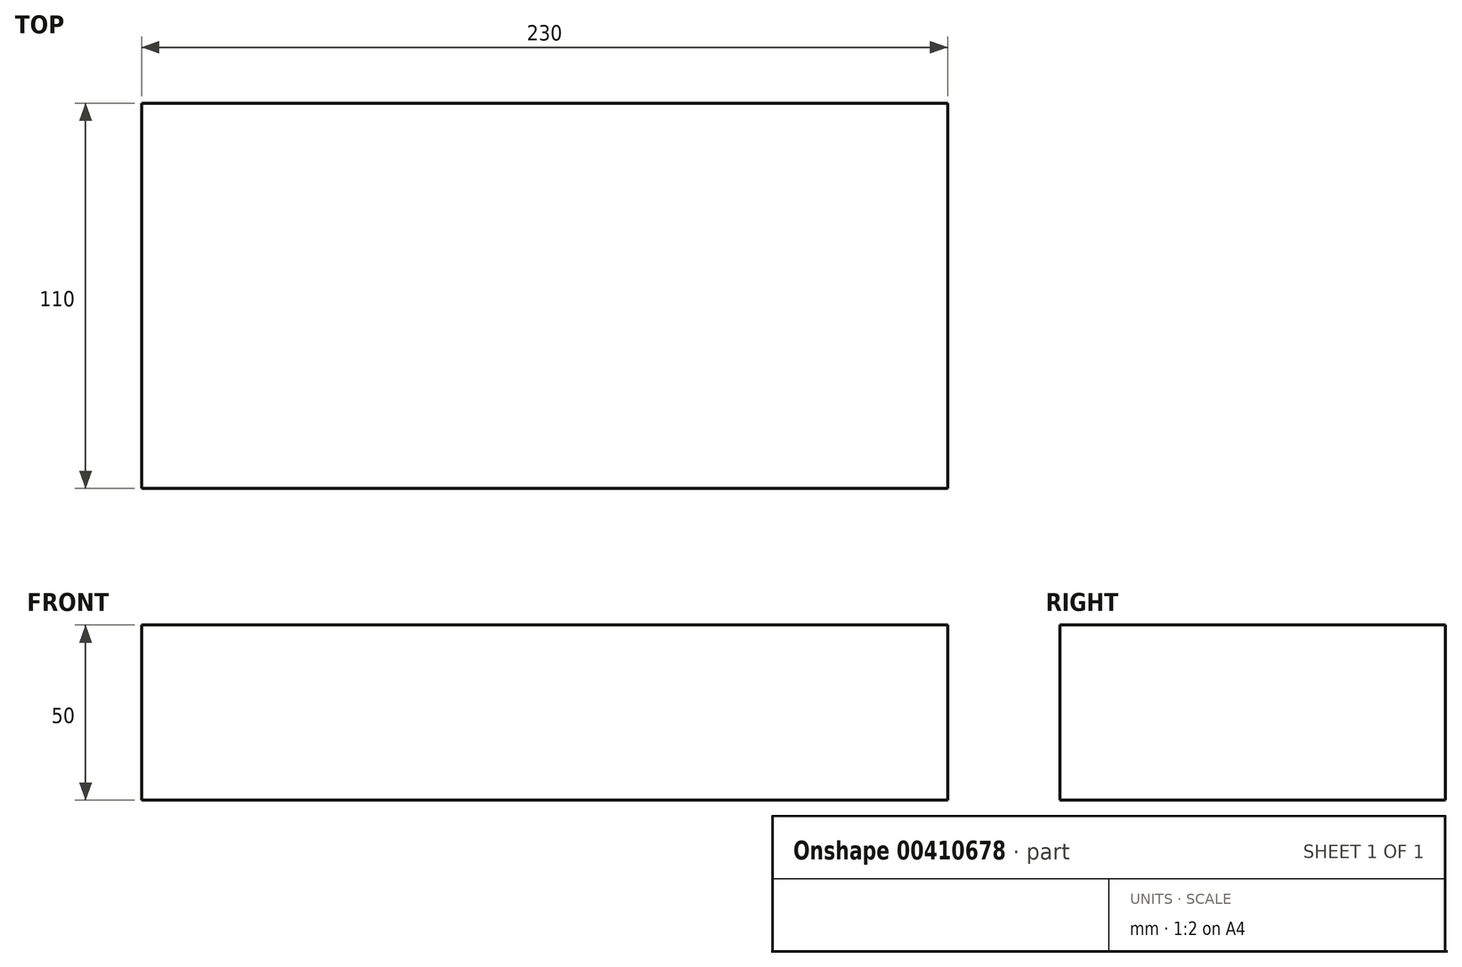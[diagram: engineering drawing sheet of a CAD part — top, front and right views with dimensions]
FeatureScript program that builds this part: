
annotation { "Feature Type Name" : "Feature", "Feature Type Description" : "" }
export const myFeature = defineFeature(function(context is Context, id is Id, definition is map)
    precondition{}
    {
        {
            var Q0;
            Q0=qCreatedBy(makeId("Front.planeOp"),FACE);
            var sketch = newSketch(context, id + "F0", { "sketchPlane" : qUnion([Q0])});
            skLineSegment(sketch, "E0.bottom", {"start": v(115, 25) * mm, "end": v(-115, 25) * mm});
            skLineSegment(sketch, "E0.top", {"start": v(115, -25) * mm, "end": v(-115, -25) * mm});
            skLineSegment(sketch, "E0.left", {"start": v(115, 25) * mm, "end": v(115, -25) * mm});
            skLineSegment(sketch, "E0.right", {"start": v(-115, 25) * mm, "end": v(-115, -25) * mm});
            skPoint(sketch, "E0.middle", {"position": v(0, 0) * mm});
            skSolve(sketch);
        }
        {
            var Q0;
            Q0=qSketchRegion(id+"F0",true);
            extrude(context, id + "F1", {"entities" : qUnion([Q0]), "endBound" : BoundingType.SYMMETRIC, "depth" : 110 * mm});
        }
    });
